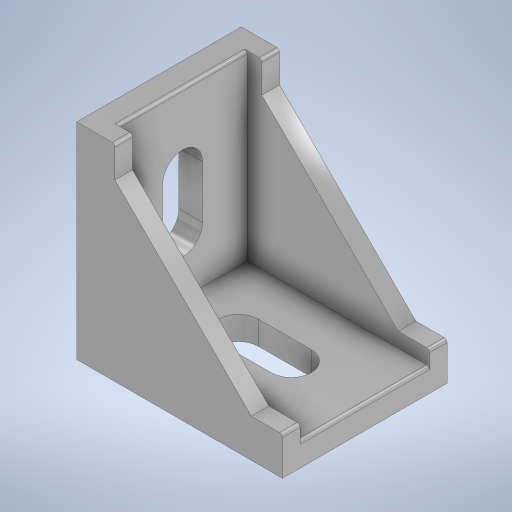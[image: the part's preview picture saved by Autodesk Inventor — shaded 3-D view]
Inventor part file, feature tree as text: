
AUTODESK INVENTOR PART (.ipt)
format: ipt  version: 2024 (Build 280153000, 153)  size: 343,040 bytes
history: native  units: mm
features: extrude x4, sketch x4, mirror x3, plane x2, fillet x1
ambient origin geometry x8: Origin, YZ Plane, XZ Plane, XY Plane, X Axis, Y Axis, Z Axis, Center Point
bodies: Solid1 (feature_tree)
feature tree (14):
  extrude  "Extrusion1"  Depth=4.0mm
  plane  "Work Plane1"
  extrude  "Extrusion2"  Depth=35.0mm
  mirror  "Mirror1"
  sketch  "Sketch3"  dims[d13=11.0mm d14=0.0mm d16=6.8mm d17=9.0mm]
  plane  "Work Plane2"
  extrude  "Extrusion3"  Depth=6.8mm
  mirror  "Mirror2"
  fillet  "Fillet1"  Radius=9.0mm
  extrude  "Extrusion4"  TaperAngle=0.0deg  [1 undecoded]
  mirror  "Mirror3"
  sketch  "Sketch1"  dims[d8=35.0mm d10=4.0mm]
  sketch  "Sketch2"  dims[d11=4.0mm d12=35.0mm]
  sketch  "Sketch4"  dims[d19=13.5mm d20=0.0mm d21=0.0mm d22=6.5mm d23=5.3mm d24=6.5mm d25=5.3mm d26=11.0mm d27=0.0mm d28=11.0mm d29=3.0mm d30=0.0mm d31=0.5mm d34=2.0mm d35=5.6mm d36=2.5mm d37=5.6mm d38=2.0mm d39=2.5mm d40=2.0mm d41=0.0mm]
note: 1 required parameter value undecoded (feature->parameter linkage not recoverable at this tier; creation-order binding heuristic only, values carry confidence <= 0.55)
